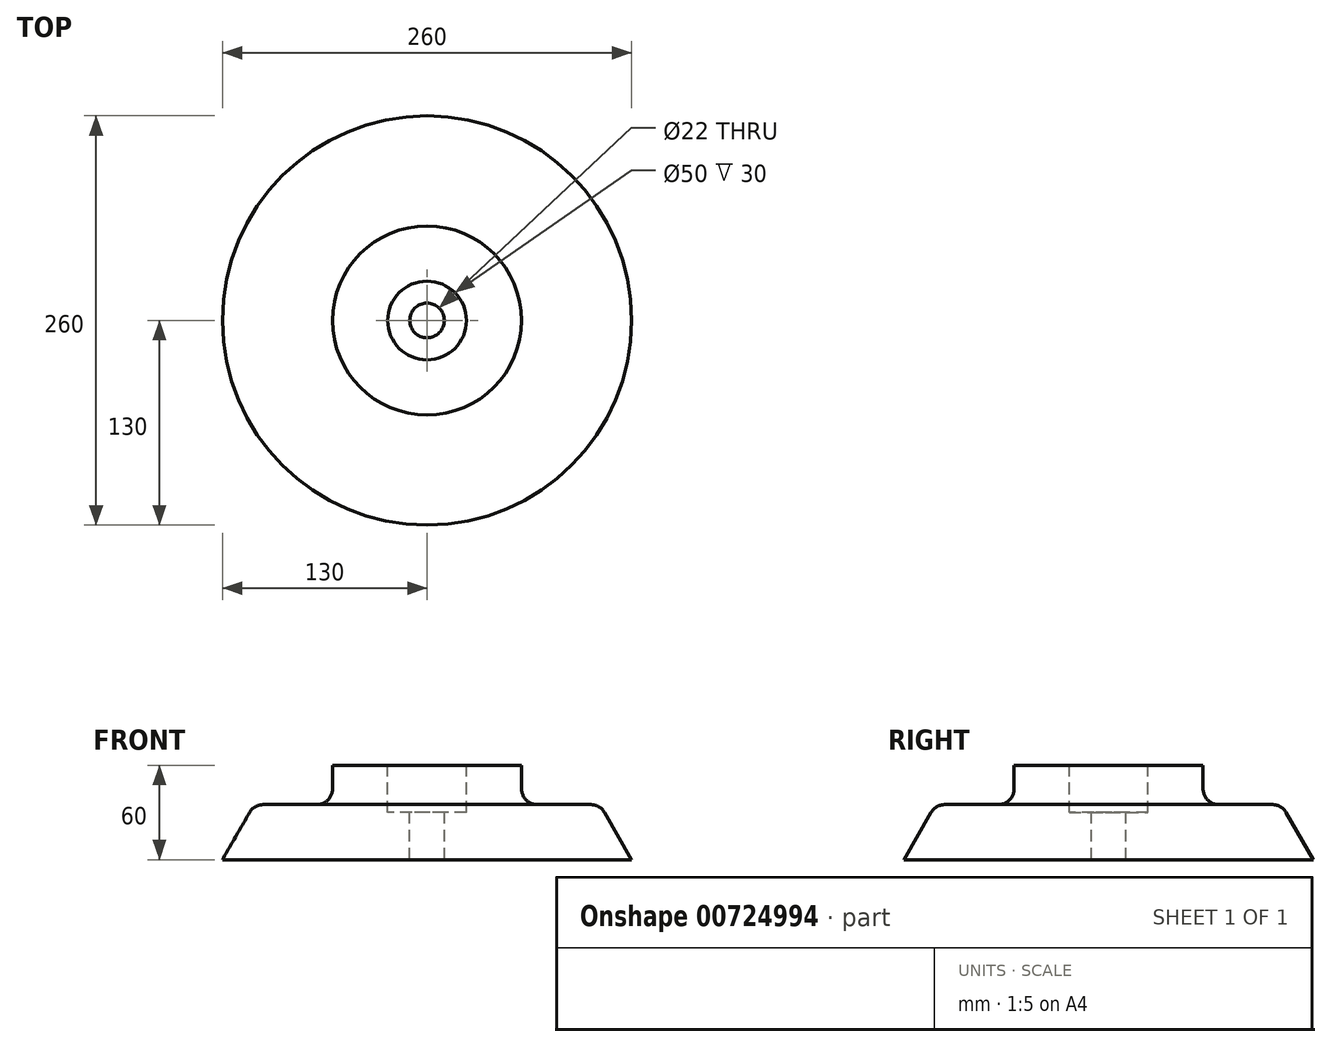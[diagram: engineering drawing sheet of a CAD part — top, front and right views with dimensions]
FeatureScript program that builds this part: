
annotation { "Feature Type Name" : "Feature", "Feature Type Description" : "" }
export const myFeature = defineFeature(function(context is Context, id is Id, definition is map)
    precondition{}
    {
        {
            var Q0;
            Q0=qCreatedBy(makeId("Front.planeOp"),FACE);
            var sketch = newSketch(context, id + "F0", { "sketchPlane" : qUnion([Q0])});
            skLineSegment(sketch, "E0", {"start": v(0, 0) * mm, "end": v(0, 60) * mm});
            skLineSegment(sketch, "E1", {"start": v(0, 60) * mm, "end": v(60, 60) * mm});
            skLineSegment(sketch, "E2", {"start": v(60, 60) * mm, "end": v(60, 35) * mm});
            skLineSegment(sketch, "E3", {"start": v(60, 35) * mm, "end": v(109.8, 35) * mm});
            skLineSegment(sketch, "E4", {"start": v(109.8, 35) * mm, "end": v(130, 0) * mm});
            skLineSegment(sketch, "E5", {"start": v(130, 0) * mm, "end": v(0, 0) * mm});
            skSolve(sketch);
        }
        {
            var Q0;
            Q0=makeQuery(id+"F0.imprint","IMPRINT",FACE,{"disambiguationData":[TD([[makeQuery(id+"F0.imprint","IMPRINT",EDGE,{"derivedFrom":sQuery(id+"F0.wireOp",EDGE,"E0")}),-1.0]])]});
            var Q1;
            Q1=sQuery(id+"F0.wireOp",EDGE,"E0");
            revolve(context, id + "F1", {"surfaceOperationType" : NewSurfaceOperationType.NEW, "entities" : qUnion([Q0]), "axis" : qUnion([Q1]), "revolveType" : RevolveType.FULL});
        }
        {
            var Q0;
            Q0=makeQuery(id+"F1.opRevolve","SWEPT_FACE",FACE,{"disambiguationData":[OSD([sQuery(id+"F0.wireOp",EDGE,"E1")])]});
            var sketch = newSketch(context, id + "F2", { "sketchPlane" : qUnion([Q0])});
            skPoint(sketch, "E6", {"position": v(0, 0) * mm});
            skSolve(sketch);
        }
        {
            var Q0;
            Q0=sQuery(id+"F2.wireOp",VERTEX,"E6");
            var Q1;
            Q1=makeQuery(id+"F1.opRevolve","SWEPT_BODY",BODY,{"disambiguationData":[OSD([sQuery(id+"F0.wireOp",EDGE,"E0"),sQuery(id+"F0.wireOp",EDGE,"E1"),sQuery(id+"F0.wireOp",EDGE,"E2"),sQuery(id+"F0.wireOp",EDGE,"E3"),sQuery(id+"F0.wireOp",EDGE,"E4"),sQuery(id+"F0.wireOp",EDGE,"E5")])]});
            hole(context, id + "F3", {"style" : HoleStyle.C_BORE, "endStyle" : HoleEndStyle.THROUGH, "holeDiameter" : 22 * mm, "cBoreDiameter" : 50 * mm, "cBoreDepth" : 30 * mm, "majorDiameter" : 5 * mm, "isTappedThrough" : true, "tappedDepth" : 12 * mm, "tapClearance" : 3, "locations" : qUnion([Q0]), "scope" : qUnion([Q1])});
        }
        {
            var Q0;
            Q0=makeQuery(id+"F1.opRevolve","SWEPT_EDGE",EDGE,{"disambiguationData":[OSD([sQuery(id+"F0.wireOp",EDGE,"E2"),sQuery(id+"F0.wireOp",EDGE,"E3")])]});
            var Q1;
            Q1=makeQuery(id+"F1.opRevolve","SWEPT_FACE",FACE,{"disambiguationData":[OSD([sQuery(id+"F0.wireOp",EDGE,"E3")])]});
            var Q2;
            Q2=makeQuery(id+"F1.opRevolve","SWEPT_EDGE",EDGE,{"disambiguationData":[OSD([sQuery(id+"F0.wireOp",EDGE,"E3"),sQuery(id+"F0.wireOp",EDGE,"E4")])]});
            fillet(context, id + "F4", {"entities" : qUnion([Q0, Q1, Q2]), "radius" : 10 * mm, "tangentPropagation" : true, "allowEdgeOverflow" : false});
        }
    });
